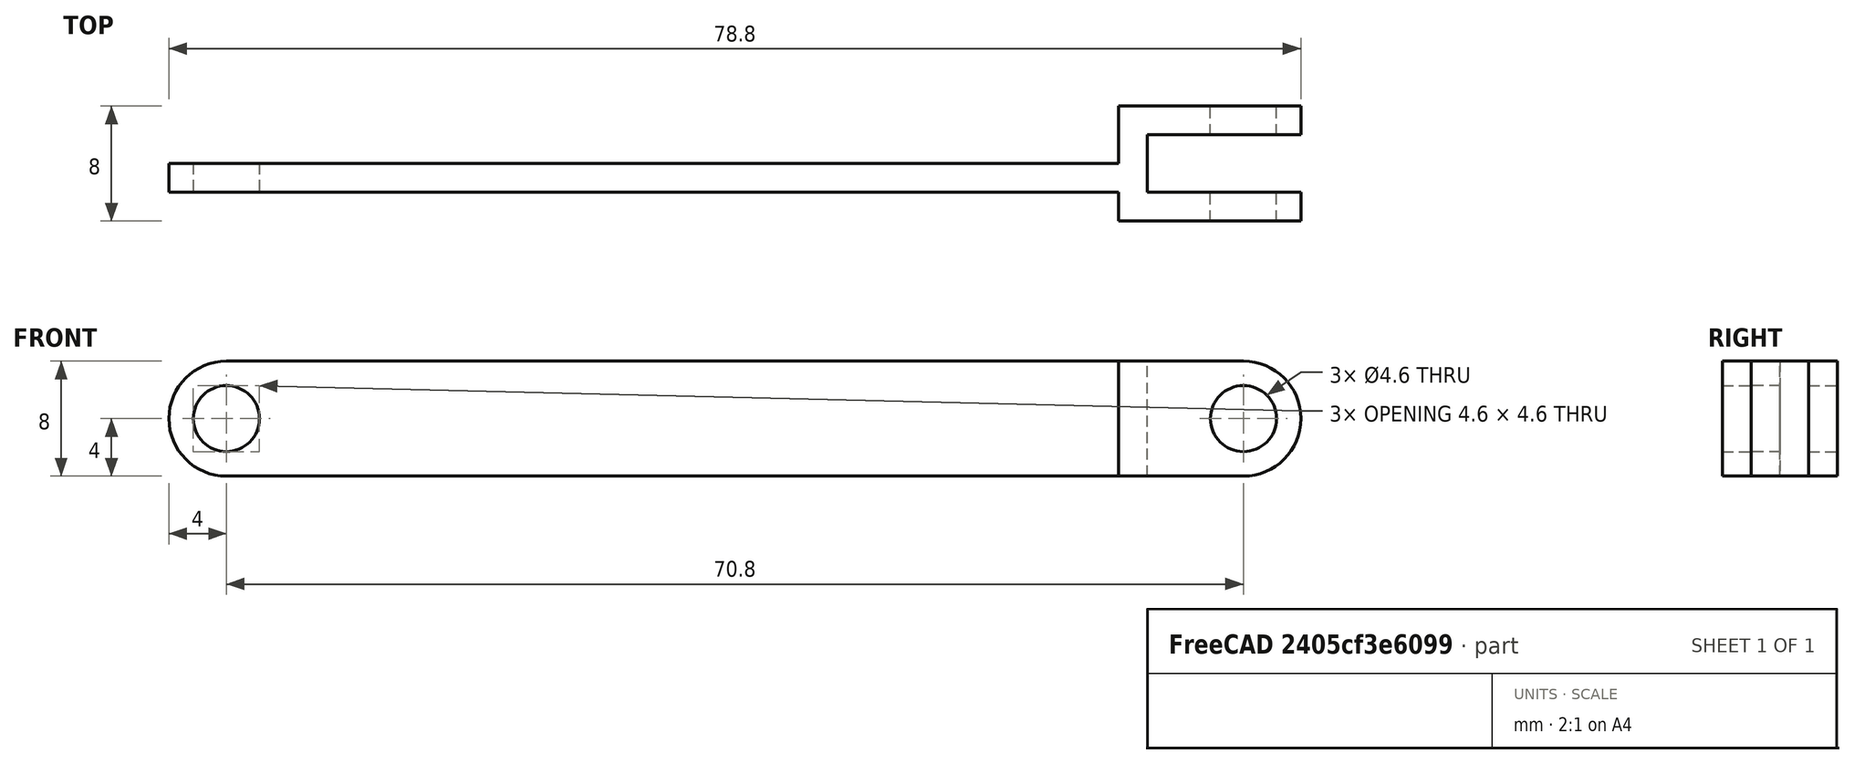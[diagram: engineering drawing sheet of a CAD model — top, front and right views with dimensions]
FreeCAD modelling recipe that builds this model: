
FCSTD DOCUMENT  (FreeCAD 0.18R16110 (Git))
Label: group arm valve
License: All rights reserved
LicenseURL: http://en.wikipedia.org/wiki/All_rights_reserved
objects: Part::Cylinder×12, Part::Cut×10, Part::Box×7, TechDraw::DrawViewDimension×5, Part::FeaturePython×4, TechDraw::DrawProjGroupItem×4, TechDraw::DrawSVGTemplate×2, TechDraw::DrawPage×2, Part::MultiFuse×1, TechDraw::DrawViewPart×1, TechDraw::DrawProjGroup×1
note: 34 computed .brp shape members not serialized (recipe doc carries the construction recipe); baked Part::Feature solids carry a one-line shape summary decoded from their .brp

FEATURE [Part::Box] Box  label="Cube"
  AttacherType = Attacher::AttachEngine3D
  Height = 8
  Length = 62.1
  Width = 2
FEATURE [Part::Cylinder] Cylinder
  Angle = 360
  AttacherType = Attacher::AttachEngine3D
  Height = 2
  Placement = pos=(0,2,4) rot=(1,0,0;1.5708rad)
  Radius = 4
FEATURE [Part::FeaturePython] BooleanFragments  # WARN: FeaturePython — macro-defined, semantics opaque (R4)
  Mode = 0
  Objects = -> [Cylinder,Box]
  Tolerance = 0
FEATURE [Part::Cylinder] Cylinder001
  Angle = 360
  AttacherType = Attacher::AttachEngine3D
  Height = 10
  Placement = pos=(0,3,4) rot=(1,0,0;1.5708rad)
  Radius = 2.3
FEATURE [Part::Cut] Cut
  Base = -> BooleanFragments
  Tool = -> Cylinder001
FEATURE [Part::Box] Box001  label="Cube001"
  AttacherType = Attacher::AttachEngine3D
  Height = 8
  Length = 2
  Placement = pos=(62.1,-2,0) rot=(0,0,1;0rad)
  Width = 8
FEATURE [Part::Cylinder] Cylinder002
  Angle = 360
  AttacherType = Attacher::AttachEngine3D
  Height = 10
  Placement = pos=(0,0,4) rot=(1,0,0;1.5708rad)
  Radius = 2.3
FEATURE [Part::Cut] Cut001
  Base = -> Cut
  Tool = -> Cylinder002
FEATURE [Part::Cylinder] Cylinder003
  Angle = 360
  AttacherType = Attacher::AttachEngine3D
  Height = 2
  Placement = pos=(0,2,4) rot=(1,0,0;1.5708rad)
  Radius = 4
FEATURE [Part::Box] Box002  label="Cube002"
  AttacherType = Attacher::AttachEngine3D
  Height = 8
  Length = 62.1
  Width = 2
FEATURE [Part::Cylinder] Cylinder004
  Angle = 360
  AttacherType = Attacher::AttachEngine3D
  Height = 10
  Placement = pos=(0,3,4) rot=(1,0,0;1.5708rad)
  Radius = 2.3
FEATURE [Part::FeaturePython] BooleanFragments001  # WARN: FeaturePython — macro-defined, semantics opaque (R4)
  Mode = 0
  Objects = -> [Cylinder003,Box002]
  Tolerance = 0
FEATURE [Part::Cut] Cut003
  Base = -> BooleanFragments001
  Tool = -> Cylinder004
FEATURE [Part::Cylinder] Cylinder005
  Angle = 360
  AttacherType = Attacher::AttachEngine3D
  Height = 10
  Placement = pos=(0,0,4) rot=(1,0,0;1.5708rad)
  Radius = 2.3
FEATURE [Part::Cut] Cut002
  Base = -> Cut003
  Placement = pos=(70.7,0,0) rot=(0,0,1;3.14159rad)
  Tool = -> Cylinder005
FEATURE [Part::Cylinder] Cylinder006
  Angle = 360
  AttacherType = Attacher::AttachEngine3D
  Height = 2
  Placement = pos=(0,2,4) rot=(1,0,0;1.5708rad)
  Radius = 4
FEATURE [Part::Box] Box003  label="Cube003"
  AttacherType = Attacher::AttachEngine3D
  Height = 8
  Length = 62.1
  Width = 2
FEATURE [Part::Cylinder] Cylinder007
  Angle = 360
  AttacherType = Attacher::AttachEngine3D
  Height = 10
  Placement = pos=(0,3,4) rot=(1,0,0;1.5708rad)
  Radius = 2.3
FEATURE [Part::FeaturePython] BooleanFragments002  # WARN: FeaturePython — macro-defined, semantics opaque (R4)
  Mode = 0
  Objects = -> [Cylinder006,Box003]
  Tolerance = 0
FEATURE [Part::Cut] Cut005
  Base = -> BooleanFragments002
  Tool = -> Cylinder007
FEATURE [Part::Cylinder] Cylinder008
  Angle = 360
  AttacherType = Attacher::AttachEngine3D
  Height = 10
  Placement = pos=(0,0,4) rot=(1,0,0;1.5708rad)
  Radius = 2.3
FEATURE [Part::Cut] Cut004
  Base = -> Cut005
  Tool = -> Cylinder008
FEATURE [Part::Box] Box004  label="Cube004"
  AttacherType = Attacher::AttachEngine3D
  Height = 8
  Length = 74
  Placement = pos=(-10,-2,0) rot=(0,0,1;0rad)
  Width = 2
FEATURE [Part::Cut] Cut006
  Base = -> Cut002
  Placement = pos=(0.1,0,0) rot=(0,0,1;0rad)
  Tool = -> Box004
FEATURE [Part::Box] Box005  label="Cube005"
  AttacherType = Attacher::AttachEngine3D
  Height = 8
  Length = 62.1
  Width = 2
FEATURE [Part::Cylinder] Cylinder009
  Angle = 360
  AttacherType = Attacher::AttachEngine3D
  Height = 2
  Placement = pos=(0,2,4) rot=(1,0,0;1.5708rad)
  Radius = 4
FEATURE [Part::FeaturePython] BooleanFragments003  # WARN: FeaturePython — macro-defined, semantics opaque (R4)
  Mode = 0
  Objects = -> [Cylinder009,Box005]
  Tolerance = 0
FEATURE [Part::Cylinder] Cylinder010
  Angle = 360
  AttacherType = Attacher::AttachEngine3D
  Height = 10
  Placement = pos=(0,3,4) rot=(1,0,0;1.5708rad)
  Radius = 2.3
FEATURE [Part::Cylinder] Cylinder011
  Angle = 360
  AttacherType = Attacher::AttachEngine3D
  Height = 10
  Placement = pos=(0,0,4) rot=(1,0,0;1.5708rad)
  Radius = 2.3
FEATURE [Part::Cut] Cut007
  Base = -> BooleanFragments003
  Tool = -> Cylinder010
FEATURE [Part::Cut] Cut009
  Base = -> Cut007
  Placement = pos=(70.7,0,0) rot=(0,0,1;3.14159rad)
  Tool = -> Cylinder011
FEATURE [Part::Box] Box006  label="Cube006"
  AttacherType = Attacher::AttachEngine3D
  Height = 8
  Length = 74
  Placement = pos=(-10,-2,0) rot=(0,0,1;0rad)
  Width = 2
FEATURE [Part::Cut] Cut008
  Base = -> Cut009
  Placement = pos=(0.1,6,0) rot=(0,0,1;0rad)
  Tool = -> Box006
FEATURE [Part::MultiFuse] Fusion
  Refine = true
  Shapes = -> [Box001,Cut001,Cut004,Cut006,Cut008]
FEATURE [TechDraw::DrawSVGTemplate] Template
  EditableTexts = Designed_by_Name=Designed by Name; Drawing_number=Drawing number; FC-Date=Date; FC-SC=Scale; FC-SH=Sheet; FC-Title=Title; Subtitle=Subtitle; Weight=Weight
  Height = 210
  Orientation = 1
  Width = 297
FEATURE [TechDraw::DrawViewPart] View
  CoarseView = false
  Direction = (0,-1,0)
  Focus = 100
  HardHidden = false
  IsoCount = 0
  IsoHidden = false
  IsoVisible = false
  LockPosition = false
  Perspective = false
  Rotation = 0
  ScaleType = 0
  SeamHidden = false
  SeamVisible = false
  SmoothHidden = false
  SmoothVisible = false
  Source = -> [Fusion]
  X = 148.5
  Y = 105
FEATURE [TechDraw::DrawPage] Page
  KeepUpdated = true
  ProjectionType = 0
  Template = -> Template
  Views = -> [View]
FEATURE [TechDraw::DrawSVGTemplate] Template001
  EditableTexts = Approved1=Approved 1; Approved2=Approved 2; CheckedBy=Checked By; Code=Code; CompanyAddress=1234 Main St; CompanyName=Company Name; DrawingNumber=Drawing Number; DrawingTitle1=Arm valve; DrawingTitle2=Drawing Title 2; DrawingTitle3=Drawing Title 3; DrawnBy=Drawn By; Revision=Rev; Scale=Scale; Sheet=Sheet n of m; Weight=Weight
  Height = 279.4
  Orientation = 1
  Width = 431.8
FEATURE [TechDraw::DrawProjGroupItem] ProjItem  label="Front"
  CoarseView = false
  Direction = (0,-1,0)
  Focus = 100
  HardHidden = false
  IsoCount = 0
  IsoHidden = false
  IsoVisible = false
  LockPosition = true
  Perspective = false
  Rotation = 0
  RotationVector = (1,0,0)
  Scale = 2
  ScaleType = 2
  SeamHidden = false
  SeamVisible = false
  SmoothHidden = false
  SmoothVisible = false
  Source = -> [Fusion]
  Type = 0
  X = 0
  Y = 0
FEATURE [TechDraw::DrawProjGroupItem] ProjItem001  label="Left"
  CoarseView = false
  Direction = (-1,-1e-16,0)
  Focus = 100
  HardHidden = false
  IsoCount = 0
  IsoHidden = false
  IsoVisible = false
  LockPosition = false
  Perspective = false
  Rotation = 0
  RotationVector = (1e-16,-1,0)
  Scale = 2
  ScaleType = 2
  SeamHidden = false
  SeamVisible = false
  SmoothHidden = false
  SmoothVisible = false
  Source = -> [Fusion]
  Type = 1
  X = 172.6
  Y = 0
FEATURE [TechDraw::DrawProjGroupItem] ProjItem002  label="FrontTopLeft"
  CoarseView = false
  Direction = (-1,-1,1)
  Focus = 100
  HardHidden = false
  IsoCount = 0
  IsoHidden = false
  IsoVisible = false
  LockPosition = false
  Perspective = false
  Rotation = 0
  RotationVector = (1,-1,0)
  Scale = 2
  ScaleType = 2
  SeamHidden = false
  SeamVisible = false
  SmoothHidden = false
  SmoothVisible = false
  Source = -> [Fusion]
  Type = 6
  X = 172.6
  Y = -172.6
FEATURE [TechDraw::DrawProjGroupItem] ProjItem003  label="Top"
  CoarseView = false
  Direction = (0,0,1)
  Focus = 100
  HardHidden = false
  IsoCount = 0
  IsoHidden = false
  IsoVisible = false
  LockPosition = false
  Perspective = false
  Rotation = 0
  RotationVector = (1,0,0)
  Scale = 2
  ScaleType = 2
  SeamHidden = false
  SeamVisible = false
  SmoothHidden = false
  SmoothVisible = false
  Source = -> [Fusion]
  Type = 4
  X = 0
  Y = -172.6
FEATURE [TechDraw::DrawProjGroup] ProjGroup
  Anchor = -> ProjItem
  AutoDistribute = true
  LockPosition = false
  ProjectionType = 0
  Rotation = 0
  Scale = 2
  ScaleType = 2
  Source = -> [Fusion]
  Views = -> [ProjItem,ProjItem001,ProjItem002,ProjItem003]
  X = 112.776
  Y = 230.626
  spacingX = 15
  spacingY = 15
FEATURE [TechDraw::DrawViewDimension] Dimension
  Arbitrary = false
  FormatSpec = %.2f
  LockPosition = false
  MeasureType = 1
  OverTolerance = 0
  References2D = -> [ProjItem]
  Rotation = 0
  ScaleType = 0
  Type = 1
  UnderTolerance = 0
  X = -8.7
  Y = -8
FEATURE [TechDraw::DrawViewDimension] Dimension001
  Arbitrary = false
  FormatSpec = %.2f
  LockPosition = false
  MeasureType = 1
  OverTolerance = 0
  References2D = -> [ProjItem]
  Rotation = 0
  ScaleType = 0
  Type = 2
  UnderTolerance = 0
  X = 70.8
  Y = 0
FEATURE [TechDraw::DrawViewDimension] Dimension002
  Arbitrary = false
  FormatSpec = %.2f
  LockPosition = false
  MeasureType = 1
  OverTolerance = 0
  References2D = -> [ProjItem001]
  Rotation = 0
  ScaleType = 0
  Type = 1
  UnderTolerance = 0
  X = 7.5e-15
  Y = -8
FEATURE [TechDraw::DrawViewDimension] Dimension003
  Arbitrary = false
  FormatSpec = %.2f
  LockPosition = false
  MeasureType = 1
  OverTolerance = 0
  References2D = -> [ProjItem001]
  Rotation = 0
  ScaleType = 0
  Type = 1
  UnderTolerance = 0
  X = 0
  Y = -8
FEATURE [TechDraw::DrawViewDimension] Dimension004
  Arbitrary = false
  FormatSpec = %.2f
  LockPosition = false
  MeasureType = 1
  OverTolerance = 0
  References2D = -> [ProjItem001]
  Rotation = 0
  ScaleType = 0
  Type = 1
  UnderTolerance = 0
  X = 2
  Y = 8
FEATURE [TechDraw::DrawPage] Page001
  KeepUpdated = true
  ProjectionType = 0
  Template = -> Template001
  Views = -> [ProjGroup,Dimension,Dimension001,Dimension002,Dimension003,Dimension004]
